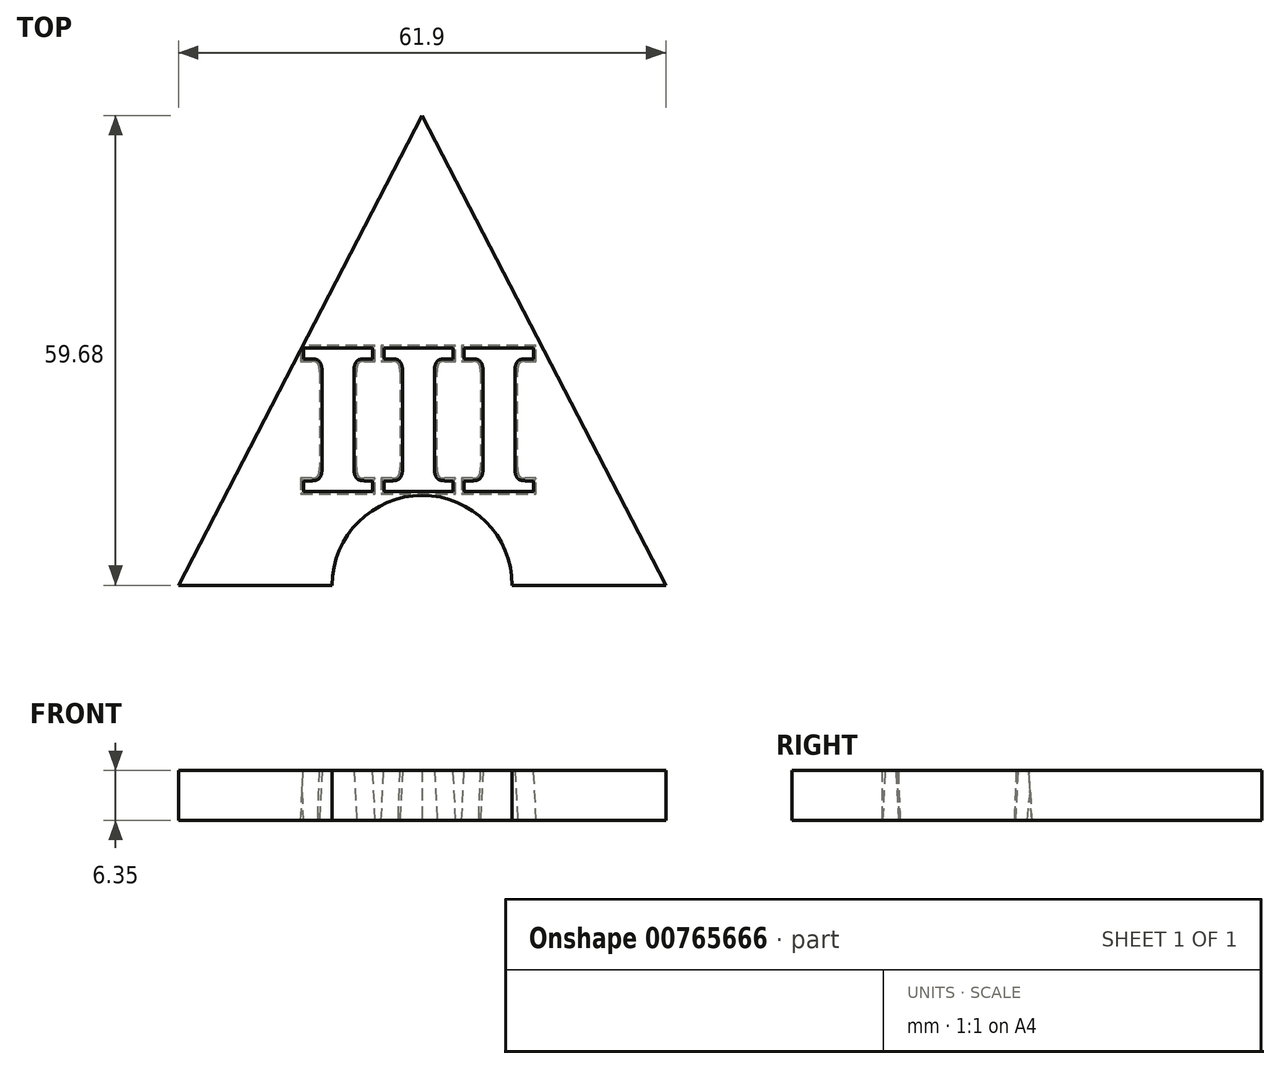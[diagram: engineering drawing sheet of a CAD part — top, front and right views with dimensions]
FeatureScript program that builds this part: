
annotation { "Feature Type Name" : "Feature", "Feature Type Description" : "" }
export const myFeature = defineFeature(function(context is Context, id is Id, definition is map)
    precondition{}
    {
        {
            var Q0;
            Q0=qCreatedBy(makeId("Top.planeOp"),FACE);
            var sketch = newSketch(context, id + "F0", { "sketchPlane" : qUnion([Q0])});
            skCircle(sketch, "E0.cCircle", {"center": v(0, 3) * mm, "radius": 17.87 * mm, "construction": true});
            skLineSegment(sketch, "E0.0", {"start": v(30.95, -14.87) * mm, "end": v(-30.95, -14.87) * mm});
            skLineSegment(sketch, "E0.1", {"start": v(-30.95, -14.87) * mm, "end": v(0, 44.81) * mm});
            skLineSegment(sketch, "E0.2", {"start": v(0, 44.81) * mm, "end": v(30.95, -14.87) * mm});
            skPoint(sketch, "E0.0.midPoint", {"position": v(0, -14.87) * mm});
            skSolve(sketch);
        }
        {
            var Q0;
            Q0=makeQuery(id+"F0.imprint","IMPRINT",FACE,{"disambiguationData":[TD([[makeQuery(id+"F0.imprint","IMPRINT",EDGE,{"derivedFrom":sQuery(id+"F0.wireOp",EDGE,"E0.0")}),-1.0]])]});
            extrude(context, id + "F1", {"entities" : qUnion([Q0]), "depth" : 6.35 * mm, "offsetDistance" : 25.4 * mm});
        }
        {
            var Q0;
            Q0=sQuery(id+"F0.wireOp",VERTEX,"E0.0.midPoint");
            var Q1;
            Q1=makeQuery(id+"F1.opExtrude","SWEPT_BODY",BODY,{"disambiguationData":[OSD([sQuery(id+"F0.wireOp",EDGE,"E0.0"),sQuery(id+"F0.wireOp",EDGE,"E0.1"),sQuery(id+"F0.wireOp",EDGE,"E0.2")])]});
            hole(context, id + "F2", {"style" : HoleStyle.SIMPLE, "endStyle" : HoleEndStyle.THROUGH, "oppositeDirection" : true, "holeDiameter" : 22.86 * mm, "majorDiameter" : 6.35 * mm, "isTappedThrough" : true, "tappedDepth" : 12.7 * mm, "tapClearance" : 3, "locations" : qUnion([Q0]), "scope" : qUnion([Q1])});
        }
        {
            var Q0;
            Q0=makeQuery(id+"F1.opExtrude","CAP_FACE",FACE,{"disambiguationData":[OSD([sQuery(id+"F0.wireOp",EDGE,"E0.0"),sQuery(id+"F0.wireOp",EDGE,"E0.1"),sQuery(id+"F0.wireOp",EDGE,"E0.2")])],"isStart":false});
            var sketch = newSketch(context, id + "F3", { "sketchPlane" : qUnion([Q0])});
            skText(sketch, "E1", { "text": "III", "fontName": "NotoSerif-Bold.ttf"});
            const initialGuessF3  = {"E1": [-0.01581, -0.00294, 1, 0, 0.01836]};
            skSetInitialGuess(sketch, initialGuessF3);
            skSolve(sketch);
        }
        {
            var Q0;
            Q0 = qSketchRegion(id + "F3", true);
            extrude(context, id + "F4", {"entities" : qUnion([Q0]), "operationType" : NewBodyOperationType.REMOVE, "oppositeDirection" : true, "depth" : 7.62 * mm, "offsetDistance" : 25.4 * mm, "hasDraft" : true, "draftAngle" : 3 * degree});
        }
    });
